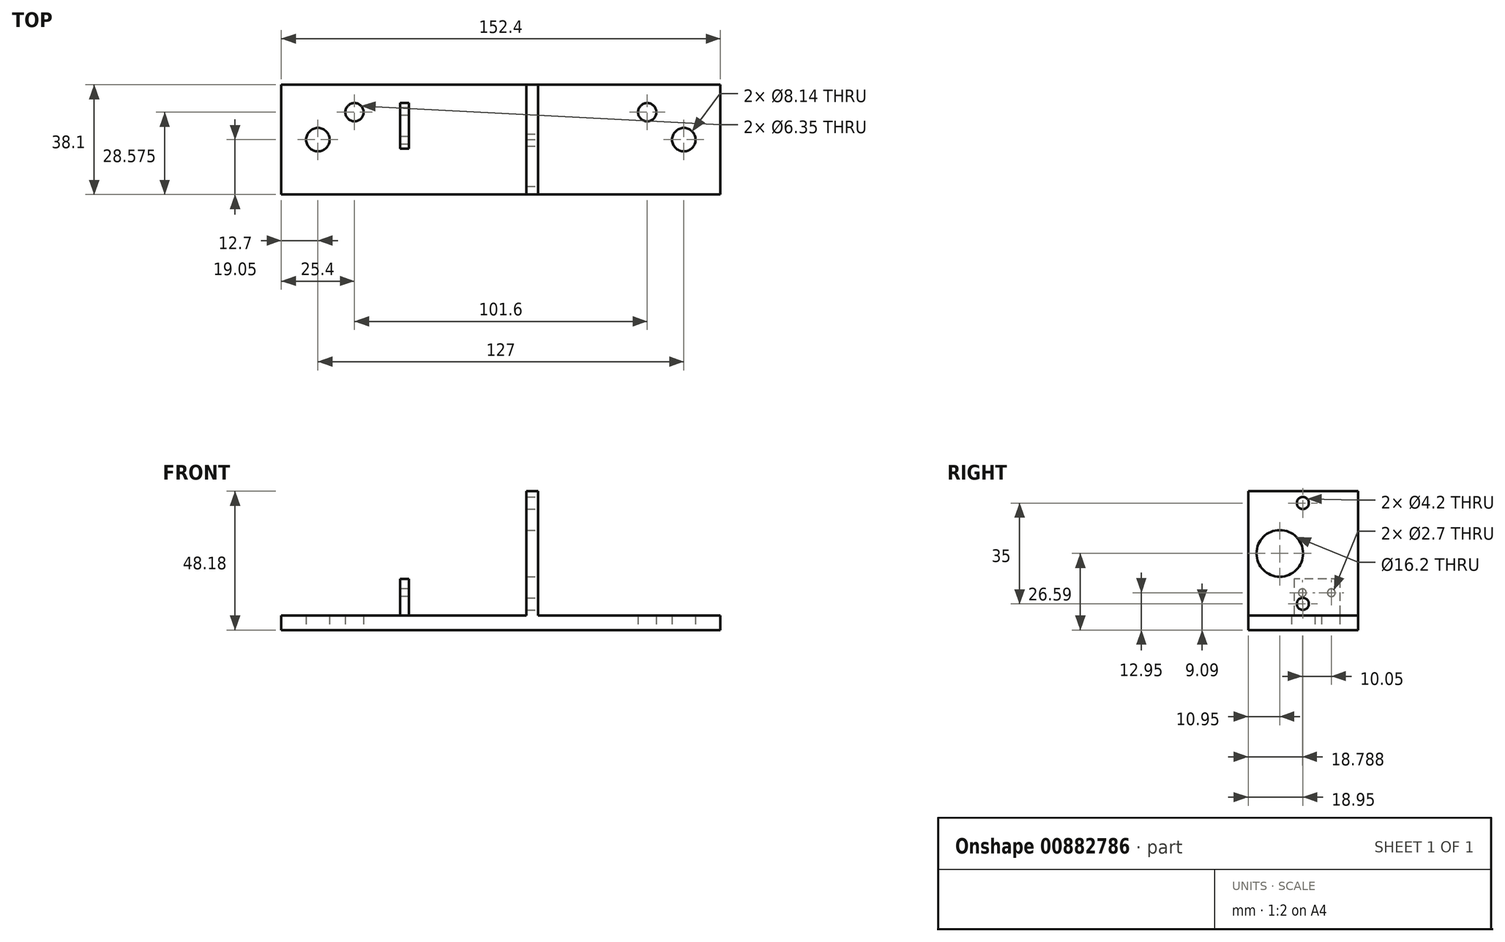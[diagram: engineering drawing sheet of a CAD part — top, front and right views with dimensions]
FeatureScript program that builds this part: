
annotation { "Feature Type Name" : "Feature", "Feature Type Description" : "" }
export const myFeature = defineFeature(function(context is Context, id is Id, definition is map)
    precondition{}
    {
        {
            var Q0;
            Q0=qCreatedBy(makeId("Top.planeOp"),FACE);
            var sketch = newSketch(context, id + "F0", { "sketchPlane" : qUnion([Q0])});
            skLineSegment(sketch, "E0.bottom", {"start": v(76.2, -19.05) * mm, "end": v(-76.2, -19.05) * mm});
            skLineSegment(sketch, "E0.top", {"start": v(76.2, 19.05) * mm, "end": v(-76.2, 19.05) * mm});
            skLineSegment(sketch, "E0.left", {"start": v(76.2, -19.05) * mm, "end": v(76.2, 19.05) * mm});
            skLineSegment(sketch, "E0.right", {"start": v(-76.2, -19.05) * mm, "end": v(-76.2, 19.05) * mm});
            skPoint(sketch, "E0.middle", {"position": v(0, 0) * mm});
            skCircle(sketch, "E1", {"center": v(-63.5, 0) * mm, "radius": 4.07 * mm});
            skCircle(sketch, "E2", {"center": v(63.5, 0) * mm, "radius": 4.07 * mm});
            skLineSegment(sketch, "E3", {"start": v(0, 19.05) * mm, "end": v(0, -19.05) * mm});
            skCircle(sketch, "E4", {"center": v(-50.8, 9.52) * mm, "radius": 3.18 * mm});
            skCircle(sketch, "E5", {"center": v(50.8, 9.52) * mm, "radius": 3.18 * mm});
            skSolve(sketch);
        }
        {
            var Q0;
            Q0 = qSketchRegion(id + "F0", true);
            extrude(context, id + "F1", {"entities" : qUnion([Q0]), "depth" : 5 * mm, "offsetDistance" : 25.4 * mm});
        }
        {
            var Q0;
            Q0=makeQuery(id+"F1.opExtrude","CAP_FACE",FACE,{"disambiguationData":[OSD([sQuery(id+"F0.wireOp",EDGE,"E0.bottom"),sQuery(id+"F0.wireOp",EDGE,"E0.top"),sQuery(id+"F0.wireOp",EDGE,"E0.left"),sQuery(id+"F0.wireOp",EDGE,"E0.right"),sQuery(id+"F0.wireOp",EDGE,"E1"),sQuery(id+"F0.wireOp",EDGE,"E2"),sQuery(id+"F0.wireOp",EDGE,"E4"),sQuery(id+"F0.wireOp",EDGE,"E5")])],"isStart":false});
            var sketch = newSketch(context, id + "F2", { "sketchPlane" : qUnion([Q0])});
            skLineSegment(sketch, "E6.bottom", {"start": v(8.89, 19.05) * mm, "end": v(12.89, 19.05) * mm});
            skLineSegment(sketch, "E6.top", {"start": v(8.9, -19.05) * mm, "end": v(12.89, -19.05) * mm});
            skLineSegment(sketch, "E6.left", {"start": v(8.89, 19.05) * mm, "end": v(8.9, -19.05) * mm});
            skLineSegment(sketch, "E6.right", {"start": v(12.89, 19.05) * mm, "end": v(12.9, -19.05) * mm});
            skLineSegment(sketch, "E7", {"start": v(-76.2, 0) * mm, "end": v(76.2, 0) * mm});
            skSolve(sketch);
        }
        {
            var Q0;
            Q0 = qSketchRegion(id + "F2", true);
            extrude(context, id + "F3", {"entities" : qUnion([Q0]), "operationType" : NewBodyOperationType.ADD, "depth" : 43.18 * mm, "offsetDistance" : 25.4 * mm});
        }
        {
            var Q0;
            {var subQ0=sQuery(id+"F0.wireOp",EDGE,"E1");var subQ1=sQuery(id+"F0.wireOp",EDGE,"E0.top");var subQ2=sQuery(id+"F0.wireOp",EDGE,"E0.right");var subQ3=sQuery(id+"F0.wireOp",EDGE,"E0.bottom");var subQ4=sQuery(id+"F0.wireOp",EDGE,"E4");Q0=makeQuery(id+"F3.boolean.opBoolean","SPLIT",FACE,{"disambiguationData":[TD([makeQuery(id+"F1.opExtrude","SWEPT_FACE",FACE,{"disambiguationData":[OSD([subQ2])]})])],"derivedFrom":makeQuery(id+"F1.opExtrude","CAP_FACE",FACE,{"disambiguationData":[OSD([subQ3,subQ1,sQuery(id+"F0.wireOp",EDGE,"E0.left"),subQ2,subQ0,sQuery(id+"F0.wireOp",EDGE,"E2"),subQ4,sQuery(id+"F0.wireOp",EDGE,"E5")])],"isStart":false})});}
            var sketch = newSketch(context, id + "F4", { "sketchPlane" : qUnion([Q0])});
            skLineSegment(sketch, "E8.bottom", {"start": v(-34.93, 12.7) * mm, "end": v(-31.93, 12.7) * mm});
            skLineSegment(sketch, "E8.top", {"start": v(-34.93, -3.18) * mm, "end": v(-31.93, -3.18) * mm});
            skLineSegment(sketch, "E8.left", {"start": v(-34.93, 12.7) * mm, "end": v(-34.93, -3.18) * mm});
            skLineSegment(sketch, "E8.right", {"start": v(-31.93, 12.7) * mm, "end": v(-31.93, -3.18) * mm});
            skSolve(sketch);
        }
        {
            var Q0;
            Q0 = qSketchRegion(id + "F4", true);
            extrude(context, id + "F5", {"entities" : qUnion([Q0]), "operationType" : NewBodyOperationType.ADD, "depth" : 12.7 * mm, "offsetDistance" : 25.4 * mm});
        }
        {
            var Q0;
            Q0=makeQuery(id+"F3.opExtrude","SWEPT_FACE",FACE,{"disambiguationData":[OSD([sQuery(id+"F2.wireOp",EDGE,"E6.right")])]});
            var sketch = newSketch(context, id + "F6", { "sketchPlane" : qUnion([Q0])});
            skCircle(sketch, "E9", {"center": v(-8.1, 26.59) * mm, "radius": 8.1 * mm});
            skCircle(sketch, "E10", {"center": v(-0.1, 9.1) * mm, "radius": 2.1 * mm});
            skCircle(sketch, "E11", {"center": v(-0.1, 44.09) * mm, "radius": 2.1 * mm});
            skLineSegment(sketch, "E12", {"start": v(-8.1, 26.59) * mm, "end": v(37.44, 26.6) * mm});
            skLineSegment(sketch, "E13", {"start": v(0, 48.18) * mm, "end": v(0, 5) * mm});
            skLineSegment(sketch, "E14", {"start": v(-19.05, 26.59) * mm, "end": v(19.05, 26.59) * mm});
            skSolve(sketch);
        }
        {
            var Q0;
            Q0 = qSketchRegion(id + "F6", true);
            extrude(context, id + "F7", {"entities" : qUnion([Q0]), "operationType" : NewBodyOperationType.REMOVE, "endBound" : BoundingType.UP_TO_NEXT, "oppositeDirection" : true, "depth" : 25.4 * mm, "offsetDistance" : 25.4 * mm});
        }
        {
            var Q0;
            Q0=makeQuery(id+"F5.opExtrude","SWEPT_FACE",FACE,{"disambiguationData":[OSD([sQuery(id+"F4.wireOp",EDGE,"E8.left")])]});
            var sketch = newSketch(context, id + "F8", { "sketchPlane" : qUnion([Q0])});
            skCircle(sketch, "E15", {"center": v(-9.79, 12.95) * mm, "radius": 1.35 * mm});
            skCircle(sketch, "E16", {"center": v(0.26, 12.95) * mm, "radius": 1.35 * mm});
            skLineSegment(sketch, "E17", {"start": v(-4.76, 17.7) * mm, "end": v(-4.76, 5) * mm});
            skSolve(sketch);
        }
        {
            var Q0;
            Q0 = qSketchRegion(id + "F8", true);
            extrude(context, id + "F9", {"entities" : qUnion([Q0]), "operationType" : NewBodyOperationType.REMOVE, "endBound" : BoundingType.UP_TO_NEXT, "oppositeDirection" : true, "depth" : 25.4 * mm, "offsetDistance" : 25.4 * mm});
        }
    });
